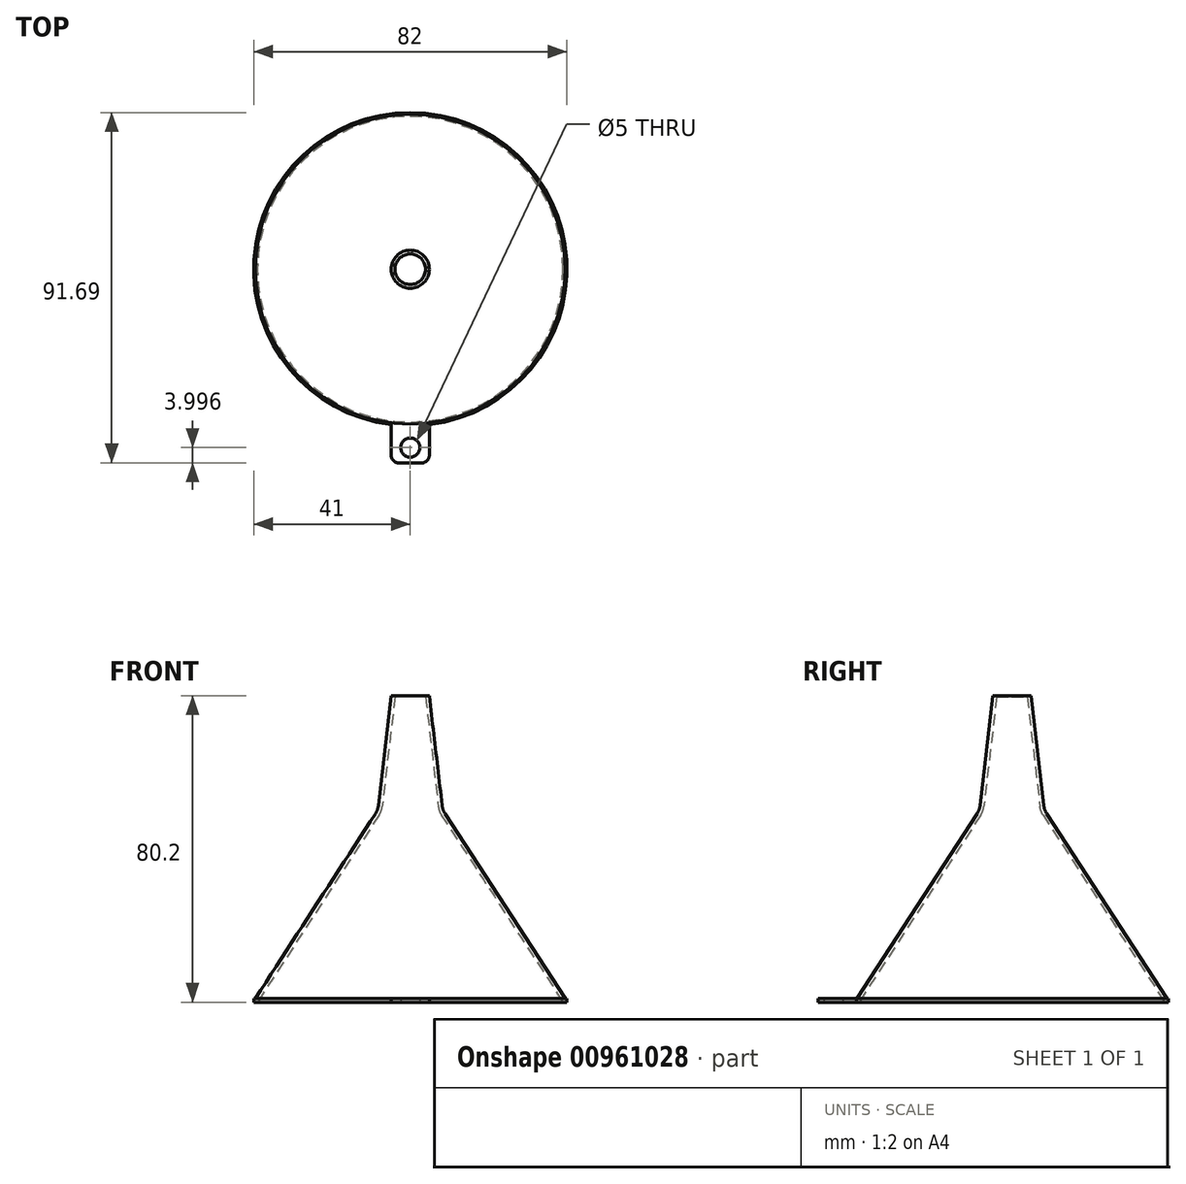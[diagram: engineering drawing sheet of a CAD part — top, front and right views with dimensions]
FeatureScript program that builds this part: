
annotation { "Feature Type Name" : "Feature", "Feature Type Description" : "" }
export const myFeature = defineFeature(function(context is Context, id is Id, definition is map)
    precondition{}
    {
        {
            var Q0;
            Q0=qCreatedBy(makeId("Front.planeOp"),FACE);
            var sketch = newSketch(context, id + "F0", { "sketchPlane" : qUnion([Q0])});
            skLineSegment(sketch, "E0", {"start": v(40, 0) * mm, "end": v(8.14, 49.02) * mm});
            skLineSegment(sketch, "E1", {"start": v(7.36, 51.16) * mm, "end": v(4, 80) * mm});
            skLineSegment(sketch, "E2.0", {"start": v(8.33, 51.51) * mm, "end": v(4.98, 80.2) * mm});
            skLineSegment(sketch, "E3.0", {"start": v(41, 0.3) * mm, "end": v(9.1, 49.37) * mm});
            skArc(sketch, "E4.filletArc", {"start": v(8.33, 51.51) * mm, "mid": v(8.6, 50.4) * mm, "end": v(9.1, 49.37) * mm});
            skPoint(sketch, "E5.visualSharp", {"position": v(7.5, 50) * mm});
            skArc(sketch, "E5.filletArc", {"start": v(7.36, 51.16) * mm, "mid": v(7.63, 50.05) * mm, "end": v(8.14, 49.02) * mm});
            skLineSegment(sketch, "E6", {"start": v(4, 80) * mm, "end": v(4.98, 80.2) * mm});
            skLineSegment(sketch, "E7", {"start": v(41, 0.3) * mm, "end": v(41, 0) * mm});
            skLineSegment(sketch, "E8", {"start": v(41, 0) * mm, "end": v(40, 0) * mm});
            skLineSegment(sketch, "E9", {"start": v(0, 73.55) * mm, "end": v(0, -22.31) * mm, "construction": true});
            skSolve(sketch);
        }
        {
            var Q0;
            Q0=makeQuery(id+"F0.imprint","IMPRINT",FACE,{"disambiguationData":[TD([[makeQuery(id+"F0.imprint","IMPRINT",EDGE,{"derivedFrom":sQuery(id+"F0.wireOp",EDGE,"E0")}),-1.0]])]});
            var Q1;
            Q1=sQuery(id+"F0.wireOp",EDGE,"E9");
            revolve(context, id + "F1", {"surfaceOperationType" : NewSurfaceOperationType.NEW, "entities" : qUnion([Q0]), "axis" : qUnion([Q1]), "revolveType" : RevolveType.FULL});
        }
        {
            var Q0;
            Q0=qCreatedBy(makeId("Top.planeOp"),FACE);
            var sketch = newSketch(context, id + "F2", { "sketchPlane" : qUnion([Q0])});
            skLineSegment(sketch, "E10", {"start": v(-5, -40.7) * mm, "end": v(-5, -48.7) * mm});
            skLineSegment(sketch, "E11", {"start": v(-3, -50.7) * mm, "end": v(0, -50.7) * mm});
            skPoint(sketch, "E12.visualSharp", {"position": v(-5, -50.7) * mm});
            skArc(sketch, "E12.filletArc", {"start": v(-5, -48.7) * mm, "mid": v(-4.41, -50.1) * mm, "end": v(-3, -50.7) * mm});
            skLineSegment(sketch, "E13.MirrorCS", {"start": v(5, -40.7) * mm, "end": v(5, -48.7) * mm});
            skArc(sketch, "E14.MirrorCS", {"start": v(5, -48.7) * mm, "mid": v(4.41, -50.1) * mm, "end": v(3, -50.7) * mm});
            skLineSegment(sketch, "E15.MirrorCS", {"start": v(3, -50.7) * mm, "end": v(0, -50.7) * mm});
            skLineSegment(sketch, "E16", {"start": v(-5, -40.7) * mm, "end": v(5, -40.7) * mm});
            skPoint(sketch, "E17", {"position": v(0, -46.7) * mm});
            skCircle(sketch, "E18", {"center": v(0, -46.7) * mm, "radius": 2.5 * mm});
            skSolve(sketch);
        }
        {
            var Q0;
            Q0=makeQuery(id+"F2.imprint","IMPRINT",FACE,{"disambiguationData":[TD([[makeQuery(id+"F2.imprint","IMPRINT",EDGE,{"derivedFrom":sQuery(id+"F2.wireOp",EDGE,"E10")}),1.0]])]});
            var Q1;
            Q1=makeQuery(id+"F1.opRevolve","SWEPT_FACE",FACE,{"disambiguationData":[OSD([sQuery(id+"F0.wireOp",EDGE,"E8")])]});
            extrude(context, id + "F3", {"entities" : qUnion([Q0, Q1]), "operationType" : NewBodyOperationType.ADD, "depth" : 1 * mm, "offsetDistance" : 25 * mm});
        }
    });
